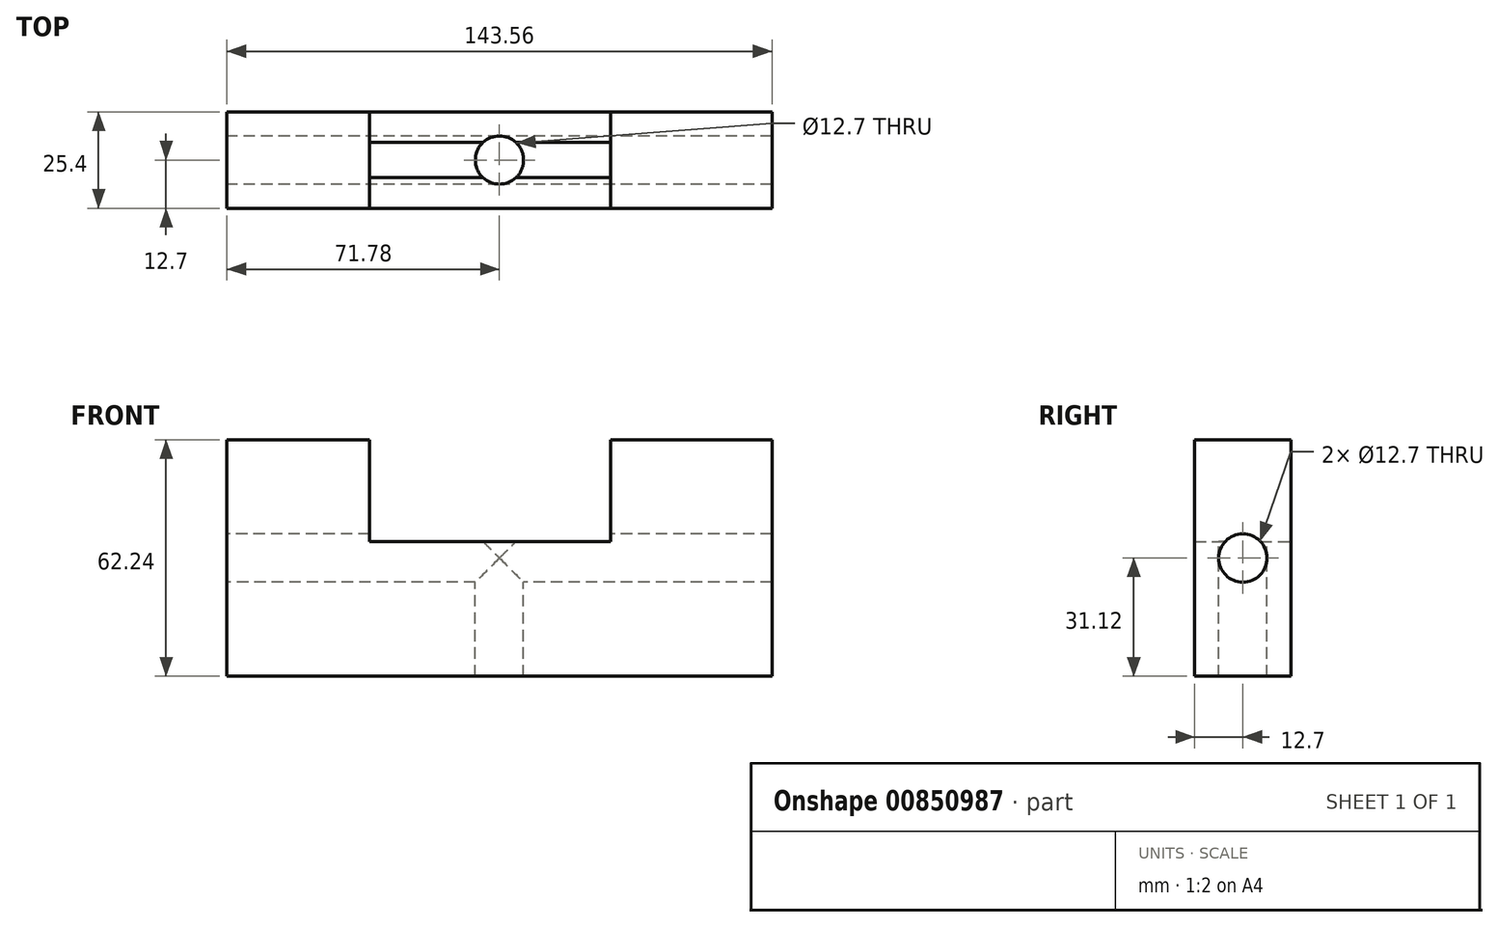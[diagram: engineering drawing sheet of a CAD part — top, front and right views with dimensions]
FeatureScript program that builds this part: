
annotation { "Feature Type Name" : "Feature", "Feature Type Description" : "" }
export const myFeature = defineFeature(function(context is Context, id is Id, definition is map)
    precondition{}
    {
        {
            var Q0;
            Q0=qCreatedBy(makeId("Front.planeOp"),FACE);
            var sketch = newSketch(context, id + "F0", { "sketchPlane" : qUnion([Q0])});
            skLineSegment(sketch, "E0.bottom", {"start": v(-71.78, 31.12) * mm, "end": v(-34.18, 31.12) * mm});
            skLineSegment(sketch, "E0.top", {"start": v(-71.78, -31.12) * mm, "end": v(71.78, -31.12) * mm});
            skLineSegment(sketch, "E0.left", {"start": v(-71.78, 31.12) * mm, "end": v(-71.78, -31.12) * mm});
            skLineSegment(sketch, "E0.right", {"start": v(71.78, 31.12) * mm, "end": v(71.78, -31.12) * mm});
            skPoint(sketch, "E0.middle", {"position": v(0, 0) * mm});
            skLineSegment(sketch, "E1", {"start": v(-34.18, 31.12) * mm, "end": v(-34.18, 4.35) * mm});
            skLineSegment(sketch, "E2", {"start": v(-34.18, 4.35) * mm, "end": v(29.29, 4.35) * mm});
            skLineSegment(sketch, "E3", {"start": v(29.29, 4.35) * mm, "end": v(29.29, 31.12) * mm});
            skLineSegment(sketch, "E4.trimOffspring", {"start": v(29.29, 31.12) * mm, "end": v(71.78, 31.12) * mm});
            skSolve(sketch);
        }
        {
            var Q0;
            Q0 = qSketchRegion(id + "F0", true);
            extrude(context, id + "F1", {"entities" : qUnion([Q0]), "depth" : 25.4 * mm, "offsetDistance" : 25.4 * mm});
        }
        {
            var Q0;
            Q0=makeQuery(id+"F1.opExtrude","SWEPT_FACE",FACE,{"disambiguationData":[OSD([sQuery(id+"F0.wireOp",EDGE,"E2")])]});
            var sketch = newSketch(context, id + "F2", { "sketchPlane" : qUnion([Q0])});
            skCircle(sketch, "E5", {"center": v(0, -12.7) * mm, "radius": 6.35 * mm});
            skPoint(sketch, "E5.centerSnap0", {"position": v(-34.18, -12.7) * mm});
            skSolve(sketch);
        }
        {
            var Q0;
            Q0=sQuery(id+"F2.wireOp",VERTEX,"E5.center");
            var Q1;
            Q1=makeQuery(id+"F1.opExtrude","SWEPT_BODY",BODY,{"disambiguationData":[OSD([sQuery(id+"F0.wireOp",EDGE,"E0.bottom"),sQuery(id+"F0.wireOp",EDGE,"E0.top"),sQuery(id+"F0.wireOp",EDGE,"E0.left"),sQuery(id+"F0.wireOp",EDGE,"E0.right"),sQuery(id+"F0.wireOp",EDGE,"E1"),sQuery(id+"F0.wireOp",EDGE,"E2"),sQuery(id+"F0.wireOp",EDGE,"E3"),sQuery(id+"F0.wireOp",EDGE,"E4.trimOffspring")])]});
            hole(context, id + "F3", {"style" : HoleStyle.SIMPLE, "endStyle" : HoleEndStyle.THROUGH, "holeDiameter" : 12.7 * mm, "majorDiameter" : 6.35 * mm, "isTappedThrough" : true, "tappedDepth" : 12.7 * mm, "tapClearance" : 3, "locations" : qUnion([Q0]), "scope" : qUnion([Q1])});
        }
        {
            var Q0;
            Q0=makeQuery(id+"F1.opExtrude","SWEPT_FACE",FACE,{"disambiguationData":[OSD([sQuery(id+"F0.wireOp",EDGE,"E0.left")])]});
            var sketch = newSketch(context, id + "F4", { "sketchPlane" : qUnion([Q0])});
            skCircle(sketch, "E6", {"center": v(12.7, 0) * mm, "radius": 6.35 * mm});
            skPoint(sketch, "E6.centerSnap0", {"position": v(12.7, 31.12) * mm});
            skSolve(sketch);
        }
        {
            var Q0;
            Q0=sQuery(id+"F4.wireOp",VERTEX,"E6.center");
            var Q1;
            Q1=makeQuery(id+"F1.opExtrude","SWEPT_BODY",BODY,{"disambiguationData":[OSD([sQuery(id+"F0.wireOp",EDGE,"E0.bottom"),sQuery(id+"F0.wireOp",EDGE,"E0.top"),sQuery(id+"F0.wireOp",EDGE,"E0.left"),sQuery(id+"F0.wireOp",EDGE,"E0.right"),sQuery(id+"F0.wireOp",EDGE,"E1"),sQuery(id+"F0.wireOp",EDGE,"E2"),sQuery(id+"F0.wireOp",EDGE,"E3"),sQuery(id+"F0.wireOp",EDGE,"E4.trimOffspring")])]});
            hole(context, id + "F5", {"style" : HoleStyle.SIMPLE, "endStyle" : HoleEndStyle.THROUGH, "holeDiameter" : 12.7 * mm, "majorDiameter" : 6.35 * mm, "isTappedThrough" : true, "tappedDepth" : 12.7 * mm, "tapClearance" : 3, "locations" : qUnion([Q0]), "scope" : qUnion([Q1])});
        }
    });
